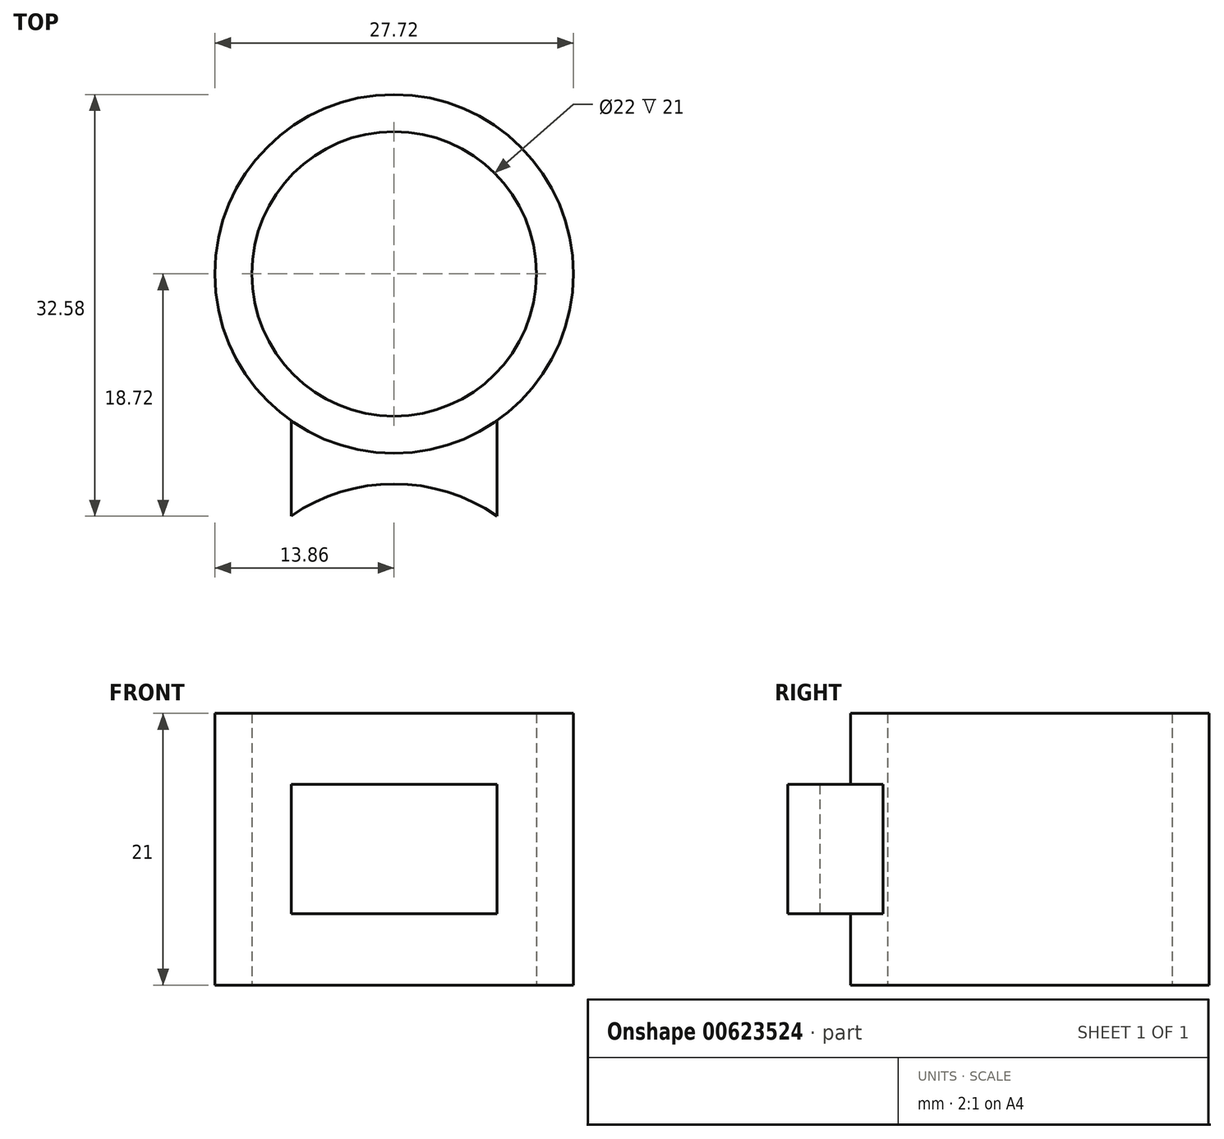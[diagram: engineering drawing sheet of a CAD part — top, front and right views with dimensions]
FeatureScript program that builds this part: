
annotation { "Feature Type Name" : "Feature", "Feature Type Description" : "" }
export const myFeature = defineFeature(function(context is Context, id is Id, definition is map)
    precondition{}
    {
        {
            var Q0;
            Q0=qCreatedBy(makeId("Top.planeOp"),FACE);
            var sketch = newSketch(context, id + "F0", { "sketchPlane" : qUnion([Q0])});
            skCircle(sketch, "E0", {"center": v(0, 0) * mm, "radius": 11 * mm});
            skCircle(sketch, "E1", {"center": v(0, 0) * mm, "radius": 13.86 * mm});
            skCircle(sketch, "E2", {"center": v(0, -30.23) * mm, "radius": 12 * mm});
            skCircle(sketch, "E3", {"center": v(0, -30.23) * mm, "radius": 14 * mm});
            skLineSegment(sketch, "E4", {"start": v(-13.06, -4.64) * mm, "end": v(13.06, -4.64) * mm});
            skLineSegment(sketch, "E5", {"start": v(0, 13.86) * mm, "end": v(0, -44.23) * mm});
            skLineSegment(sketch, "E6", {"start": v(7.96, -11.35) * mm, "end": v(7.96, -18.72) * mm});
            skLineSegment(sketch, "E7", {"start": v(-7.96, -18.72) * mm, "end": v(-7.96, -11.35) * mm});
            skSolve(sketch);
        }
        {
            var Q0;
            {var subQ0=sQuery(id+"F0.wireOp",EDGE,"E4");var subQ1=sQuery(id+"F0.wireOp",EDGE,"E0");var subQ2=makeQuery(id+"F0.imprint","INTERSECT",VERTEX,{"disambiguationData":[OD(0.0)],"derivedFrom":[subQ1,subQ0]});Q0=makeQuery(id+"F0.imprint","IMPRINT",FACE,{"disambiguationData":[TD([[makeQuery(id+"F0.imprint","IMPRINT",EDGE,{"disambiguationData":[TD([[subQ2,1.0]])],"derivedFrom":subQ1}),-1.0]])]});}
            var Q1;
            {var subQ0=sQuery(id+"F0.wireOp",EDGE,"E5");var subQ1=sQuery(id+"F0.wireOp",EDGE,"E0");var subQ2=makeQuery(id+"F0.imprint","INTERSECT",VERTEX,{"disambiguationData":[OD(0.0)],"derivedFrom":[subQ1,subQ0]});Q1=makeQuery(id+"F0.imprint","IMPRINT",FACE,{"disambiguationData":[TD([[makeQuery(id+"F0.imprint","IMPRINT",EDGE,{"disambiguationData":[TD([[subQ2,1.0]])],"derivedFrom":subQ1}),-1.0]])]});}
            var Q2;
            {var subQ0=sQuery(id+"F0.wireOp",EDGE,"E5");var subQ1=sQuery(id+"F0.wireOp",EDGE,"E0");var subQ2=makeQuery(id+"F0.imprint","INTERSECT",VERTEX,{"disambiguationData":[OD(1.0)],"derivedFrom":[subQ1,subQ0]});Q2=makeQuery(id+"F0.imprint","IMPRINT",FACE,{"disambiguationData":[TD([[makeQuery(id+"F0.imprint","IMPRINT",EDGE,{"disambiguationData":[TD([[subQ2,-1.0]])],"derivedFrom":subQ1}),-1.0]])]});}
            var Q3;
            {var subQ0=sQuery(id+"F0.wireOp",EDGE,"E4");var subQ1=sQuery(id+"F0.wireOp",EDGE,"E0");var subQ2=makeQuery(id+"F0.imprint","INTERSECT",VERTEX,{"disambiguationData":[OD(0.0)],"derivedFrom":[subQ1,subQ0]});Q3=makeQuery(id+"F0.imprint","IMPRINT",FACE,{"disambiguationData":[TD([[makeQuery(id+"F0.imprint","IMPRINT",EDGE,{"disambiguationData":[TD([[subQ2,-1.0]])],"derivedFrom":subQ1}),-1.0]])]});}
            extrude(context, id + "F1", {"entities" : qUnion([Q0, Q1, Q2, Q3]), "depth" : 10.5 * mm, "offsetDistance" : 25 * mm});
        }
        {
            var Q0;
            {var subQ0=sQuery(id+"F0.wireOp",EDGE,"E5");var subQ1=sQuery(id+"F0.wireOp",EDGE,"E0");var subQ2=makeQuery(id+"F0.imprint","INTERSECT",VERTEX,{"disambiguationData":[OD(0.0)],"derivedFrom":[subQ1,subQ0]});Q0=makeQuery(id+"F0.imprint","IMPRINT",FACE,{"disambiguationData":[TD([[makeQuery(id+"F0.imprint","IMPRINT",EDGE,{"disambiguationData":[TD([[subQ2,1.0]])],"derivedFrom":subQ1}),-1.0]])]});}
            var Q1;
            {var subQ0=sQuery(id+"F0.wireOp",EDGE,"E4");var subQ1=sQuery(id+"F0.wireOp",EDGE,"E0");var subQ2=makeQuery(id+"F0.imprint","INTERSECT",VERTEX,{"disambiguationData":[OD(0.0)],"derivedFrom":[subQ1,subQ0]});Q1=makeQuery(id+"F0.imprint","IMPRINT",FACE,{"disambiguationData":[TD([[makeQuery(id+"F0.imprint","IMPRINT",EDGE,{"disambiguationData":[TD([[subQ2,1.0]])],"derivedFrom":subQ1}),-1.0]])]});}
            var Q2;
            {var subQ0=sQuery(id+"F0.wireOp",EDGE,"E5");var subQ1=sQuery(id+"F0.wireOp",EDGE,"E0");var subQ2=makeQuery(id+"F0.imprint","INTERSECT",VERTEX,{"disambiguationData":[OD(1.0)],"derivedFrom":[subQ1,subQ0]});Q2=makeQuery(id+"F0.imprint","IMPRINT",FACE,{"disambiguationData":[TD([[makeQuery(id+"F0.imprint","IMPRINT",EDGE,{"disambiguationData":[TD([[subQ2,-1.0]])],"derivedFrom":subQ1}),-1.0]])]});}
            var Q3;
            {var subQ0=sQuery(id+"F0.wireOp",EDGE,"E4");var subQ1=sQuery(id+"F0.wireOp",EDGE,"E0");var subQ2=makeQuery(id+"F0.imprint","INTERSECT",VERTEX,{"disambiguationData":[OD(0.0)],"derivedFrom":[subQ1,subQ0]});Q3=makeQuery(id+"F0.imprint","IMPRINT",FACE,{"disambiguationData":[TD([[makeQuery(id+"F0.imprint","IMPRINT",EDGE,{"disambiguationData":[TD([[subQ2,-1.0]])],"derivedFrom":subQ1}),-1.0]])]});}
            extrude(context, id + "F2", {"entities" : qUnion([Q0, Q1, Q2, Q3]), "operationType" : NewBodyOperationType.ADD, "oppositeDirection" : true, "depth" : 10.5 * mm, "offsetDistance" : 25 * mm});
        }
        {
            var Q0;
            {var subQ0=sQuery(id+"F0.wireOp",EDGE,"E7");Q0=makeQuery(id+"F0.imprint","IMPRINT",FACE,{"disambiguationData":[TD([[makeQuery(id+"F0.imprint","IMPRINT",EDGE,{"derivedFrom":subQ0}),-1.0]])]});}
            var Q1;
            {var subQ0=sQuery(id+"F0.wireOp",EDGE,"E6");Q1=makeQuery(id+"F0.imprint","IMPRINT",FACE,{"disambiguationData":[TD([[makeQuery(id+"F0.imprint","IMPRINT",EDGE,{"derivedFrom":subQ0}),-1.0]])]});}
            extrude(context, id + "F3", {"entities" : qUnion([Q0, Q1]), "operationType" : NewBodyOperationType.ADD, "depth" : 5 * mm, "offsetDistance" : 25 * mm});
        }
        {
            var Q0;
            {var subQ0=sQuery(id+"F0.wireOp",EDGE,"E7");Q0=makeQuery(id+"F0.imprint","IMPRINT",FACE,{"disambiguationData":[TD([[makeQuery(id+"F0.imprint","IMPRINT",EDGE,{"derivedFrom":subQ0}),-1.0]])]});}
            var Q1;
            {var subQ0=sQuery(id+"F0.wireOp",EDGE,"E6");Q1=makeQuery(id+"F0.imprint","IMPRINT",FACE,{"disambiguationData":[TD([[makeQuery(id+"F0.imprint","IMPRINT",EDGE,{"derivedFrom":subQ0}),-1.0]])]});}
            extrude(context, id + "F4", {"entities" : qUnion([Q0, Q1]), "operationType" : NewBodyOperationType.ADD, "oppositeDirection" : true, "depth" : 5 * mm, "offsetDistance" : 25 * mm});
        }
    });
